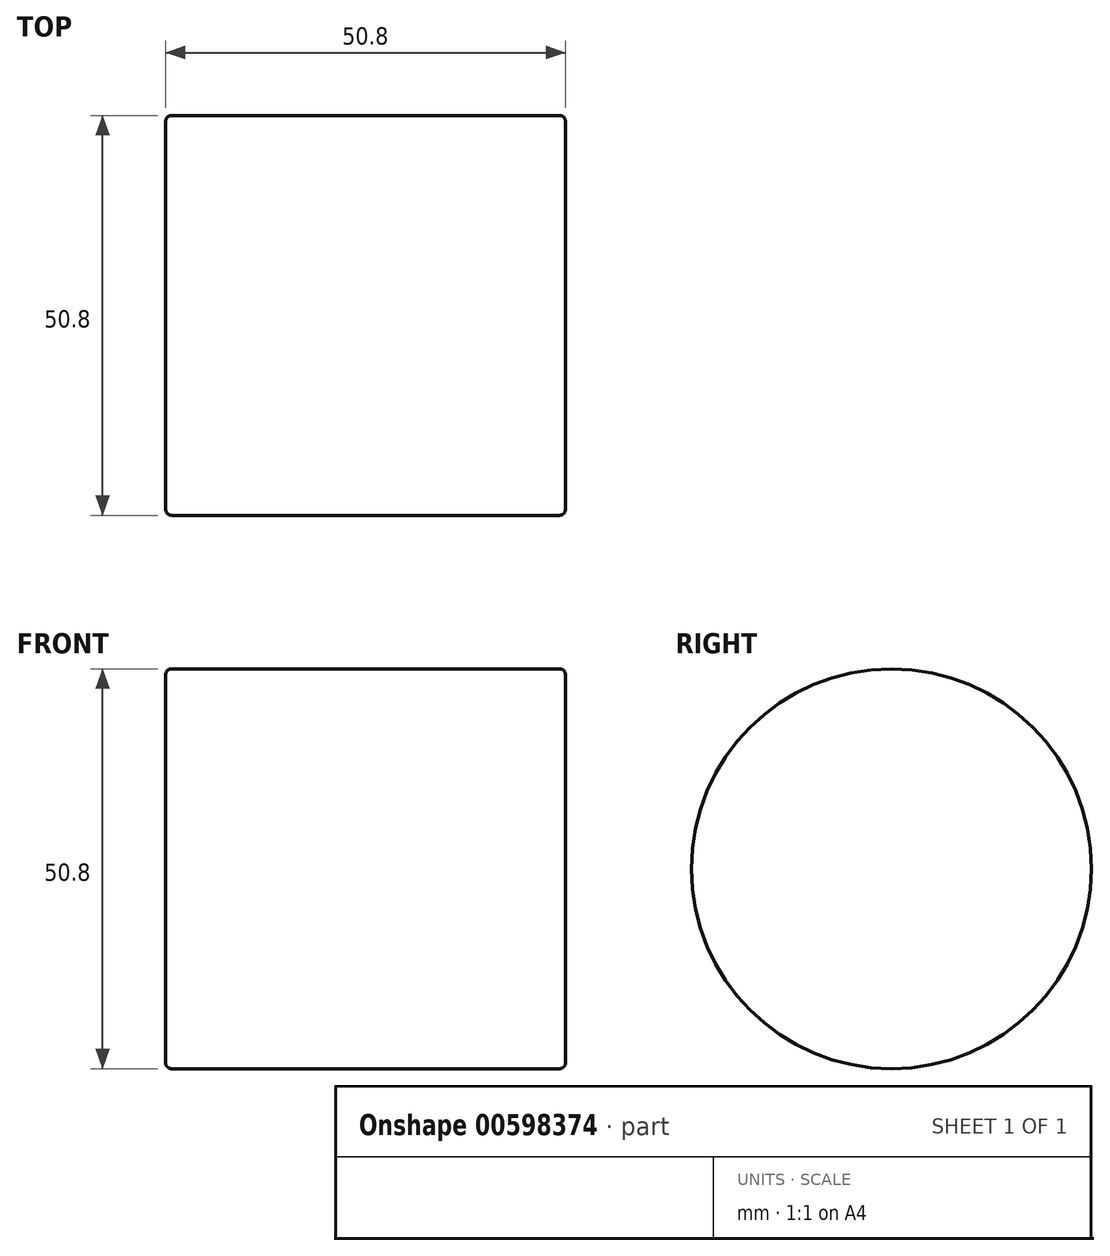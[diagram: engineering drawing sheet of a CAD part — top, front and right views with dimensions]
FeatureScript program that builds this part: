
annotation { "Feature Type Name" : "Feature", "Feature Type Description" : "" }
export const myFeature = defineFeature(function(context is Context, id is Id, definition is map)
    precondition{}
    {
        {
            var Q0;
            Q0=qCreatedBy(makeId("Right.planeOp"),FACE);
            var sketch = newSketch(context, id + "F0", { "sketchPlane" : qUnion([Q0])});
            skCircle(sketch, "E0", {"center": v(0, 0) * mm, "radius": 25.4 * mm});
            skSolve(sketch);
        }
        {
            var Q0;
            Q0 = qSketchRegion(id + "F0", true);
            extrude(context, id + "F1", {"entities" : qUnion([Q0]), "endBound" : BoundingType.SYMMETRIC, "depth" : 50.8 * mm, "offsetDistance" : 25.4 * mm});
        }
        {
            var Q0;
            Q0=makeQuery(id+"F1.opExtrude","CAP_EDGE",EDGE,{"disambiguationData":[OSD([sQuery(id+"F0.wireOp",EDGE,"E0")])],"isStart":false});
            var Q1;
            Q1=makeQuery(id+"F1.opExtrude","CAP_EDGE",EDGE,{"disambiguationData":[OSD([sQuery(id+"F0.wireOp",EDGE,"E0")])],"isStart":true});
            fillet(context, id + "F2", {"entities" : qUnion([Q0, Q1]), "radius" : 0.76 * mm, "tangentPropagation" : true, "allowEdgeOverflow" : false});
        }
    });
